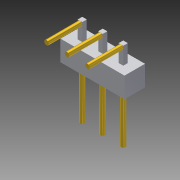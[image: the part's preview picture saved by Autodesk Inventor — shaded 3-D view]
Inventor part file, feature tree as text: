
AUTODESK INVENTOR PART (.ipt)
format: ipt  version: 2014 SP1 (Build 180222100, 222)  size: 103,936 bytes
history: native  units: in
note: dims shown in document units (in); Inventor stores cm internally (conversion verified against a paired STEP export)
features: extrude x1, imported_body x1
ambient origin geometry x8: Origin, YZ Plane, XZ Plane, XY Plane, X Axis, Y Axis, Z Axis, Center Point
bodies: Body1 (feature_tree)
feature tree (2):
  extrude  "Extrude4"  [1 undecoded]
  imported_body  "Base1"
note: 1 required parameter value undecoded (feature->parameter linkage not recoverable at this tier; creation-order binding heuristic only, values carry confidence <= 0.55)
